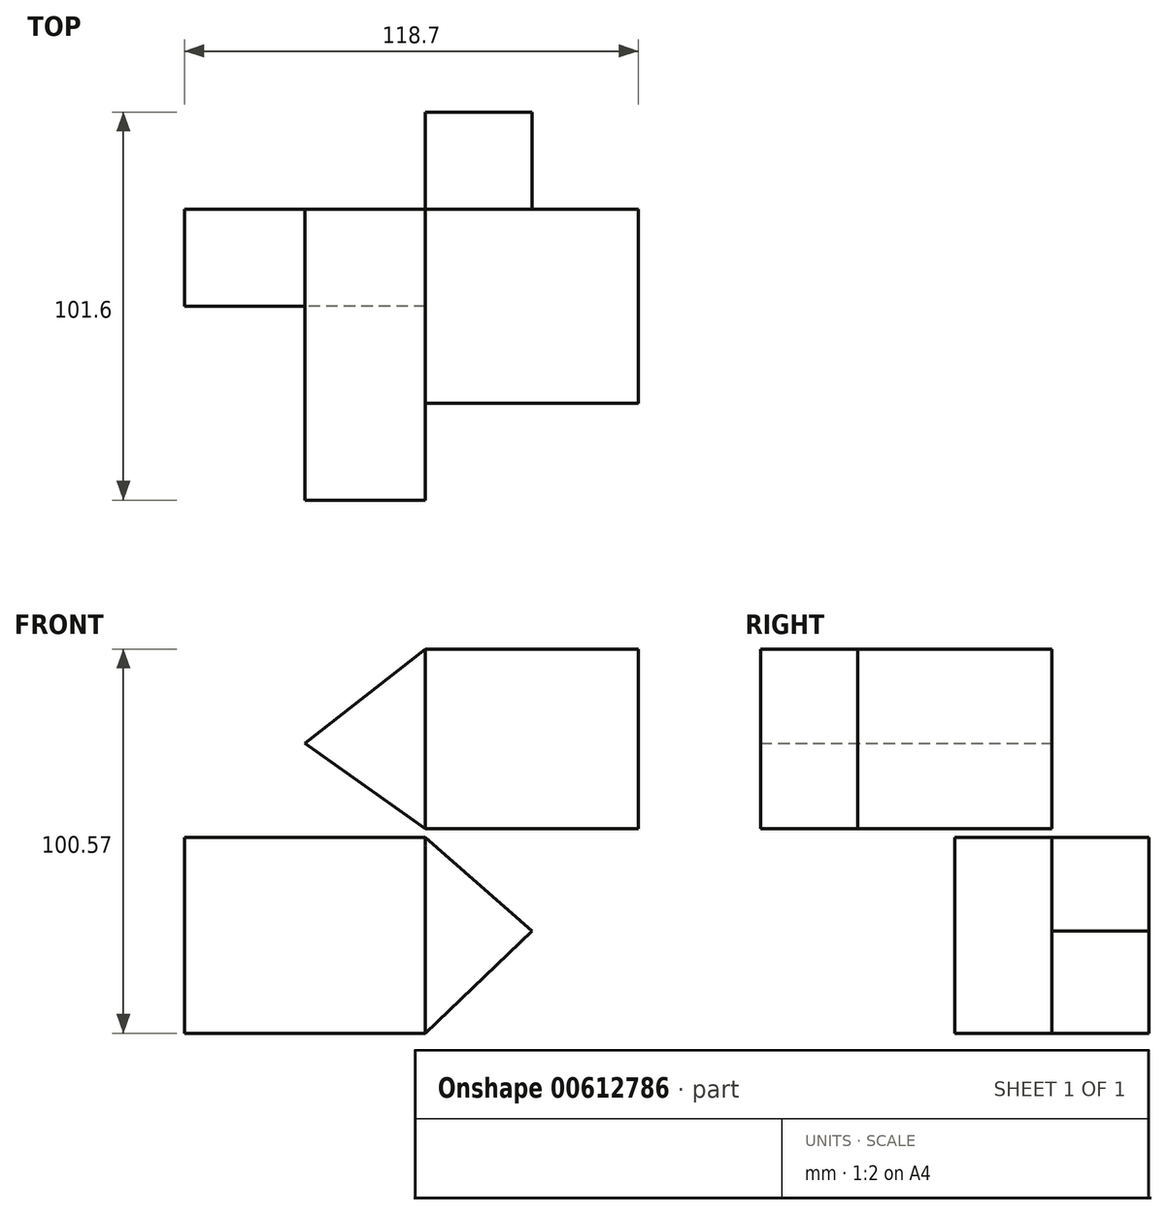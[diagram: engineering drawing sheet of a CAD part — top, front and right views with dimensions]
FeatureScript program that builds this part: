
annotation { "Feature Type Name" : "Feature", "Feature Type Description" : "" }
export const myFeature = defineFeature(function(context is Context, id is Id, definition is map)
    precondition{}
    {
        {
            var Q0;
            Q0=qCreatedBy(makeId("Front.planeOp"),FACE);
            var sketch = newSketch(context, id + "F0", { "sketchPlane" : qUnion([Q0])});
            skLineSegment(sketch, "E0.bottom", {"start": v(0, 0) * mm, "end": v(55.67, 0) * mm});
            skLineSegment(sketch, "E0.top", {"start": v(0, 47.03) * mm, "end": v(55.67, 47.03) * mm});
            skLineSegment(sketch, "E0.left", {"start": v(0, 0) * mm, "end": v(0, 47.03) * mm});
            skLineSegment(sketch, "E0.right", {"start": v(55.67, 0) * mm, "end": v(55.67, 47.03) * mm});
            skLineSegment(sketch, "E1.bottom", {"start": v(0, -2.27) * mm, "end": v(-63.03, -2.27) * mm});
            skLineSegment(sketch, "E1.top", {"start": v(0, -53.54) * mm, "end": v(-63.03, -53.54) * mm});
            skLineSegment(sketch, "E1.left", {"start": v(0, -2.27) * mm, "end": v(0, -53.54) * mm});
            skLineSegment(sketch, "E1.right", {"start": v(-63.03, -2.27) * mm, "end": v(-63.03, -53.54) * mm});
            skLineSegment(sketch, "E2", {"start": v(0, -53.54) * mm, "end": v(55.67, 0) * mm});
            skLineSegment(sketch, "E3", {"start": v(-63.03, -2.27) * mm, "end": v(0, 47.03) * mm});
            skLineSegment(sketch, "E4", {"start": v(0, -2.27) * mm, "end": v(27.83, -26.77) * mm});
            skLineSegment(sketch, "E5", {"start": v(0, 0) * mm, "end": v(-31.52, 22.38) * mm});
            skSolve(sketch);
        }
        {
            var Q0;
            Q0=makeQuery(id+"F0.imprint","IMPRINT",FACE,{"disambiguationData":[TD([[makeQuery(id+"F0.imprint","IMPRINT",EDGE,{"derivedFrom":sQuery(id+"F0.wireOp",EDGE,"E1.bottom")}),1.0]])]});
            extrude(context, id + "F1", {"entities" : qUnion([Q0]), "depth" : 25.4 * mm, "offsetDistance" : 25.4 * mm});
        }
        {
            var Q0;
            Q0=makeQuery(id+"F0.imprint","IMPRINT",FACE,{"disambiguationData":[TD([[makeQuery(id+"F0.imprint","IMPRINT",EDGE,{"derivedFrom":sQuery(id+"F0.wireOp",EDGE,"E0.bottom")}),1.0]])]});
            extrude(context, id + "F2", {"entities" : qUnion([Q0]), "depth" : 50.8 * mm, "offsetDistance" : 25.4 * mm});
        }
        {
            var Q0;
            {var subQ0=sQuery(id+"F0.wireOp",EDGE,"E0.left");Q0=makeQuery(id+"F0.imprint","IMPRINT",FACE,{"disambiguationData":[TD([[makeQuery(id+"F0.imprint","IMPRINT",EDGE,{"derivedFrom":subQ0}),1.0]])]});}
            extrude(context, id + "F3", {"entities" : qUnion([Q0]), "operationType" : NewBodyOperationType.ADD, "depth" : 76.2 * mm, "offsetDistance" : 25.4 * mm});
        }
        {
            var Q0;
            {var subQ0=sQuery(id+"F0.wireOp",EDGE,"E1.left");Q0=makeQuery(id+"F0.imprint","IMPRINT",FACE,{"disambiguationData":[TD([[makeQuery(id+"F0.imprint","IMPRINT",EDGE,{"derivedFrom":subQ0}),1.0]])]});}
            extrude(context, id + "F4", {"entities" : qUnion([Q0]), "operationType" : NewBodyOperationType.ADD, "oppositeDirection" : true, "depth" : 25.4 * mm, "offsetDistance" : 25.4 * mm});
        }
    });
